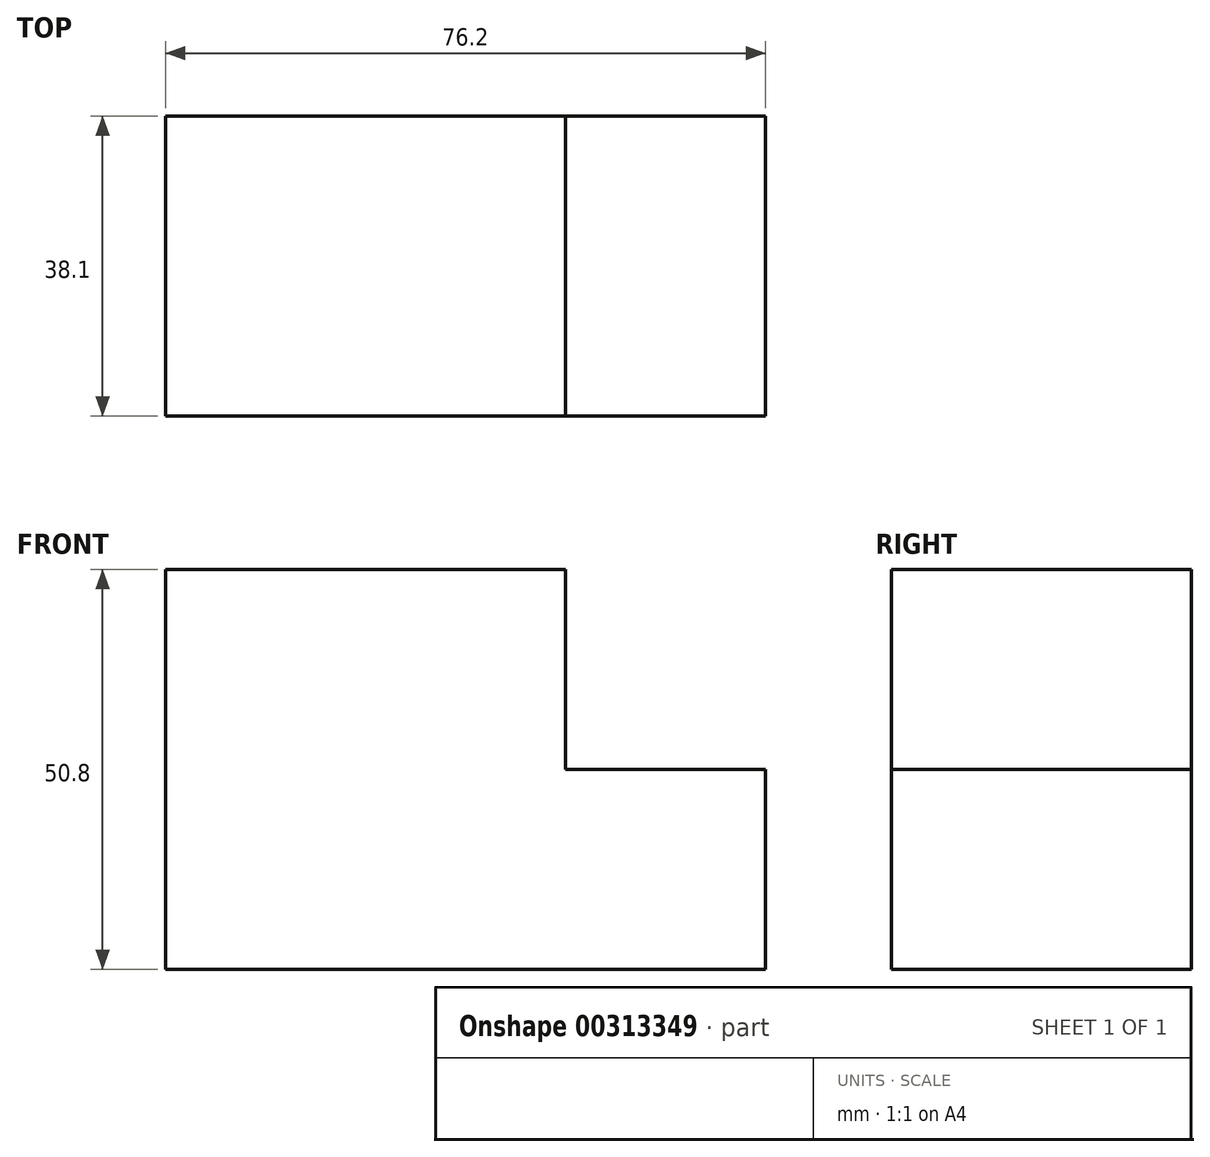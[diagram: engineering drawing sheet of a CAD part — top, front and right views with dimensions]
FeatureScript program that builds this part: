
annotation { "Feature Type Name" : "Feature", "Feature Type Description" : "" }
export const myFeature = defineFeature(function(context is Context, id is Id, definition is map)
    precondition{}
    {
        {
            var Q0;
            Q0=qCreatedBy(makeId("Front.planeOp"),FACE);
            var sketch = newSketch(context, id + "F0", { "sketchPlane" : qUnion([Q0])});
            skLineSegment(sketch, "E0", {"start": v(-37.44, -34.69) * mm, "end": v(38.76, -34.69) * mm});
            skLineSegment(sketch, "E1", {"start": v(38.76, -34.69) * mm, "end": v(38.76, -9.29) * mm});
            skLineSegment(sketch, "E2", {"start": v(38.76, -9.29) * mm, "end": v(13.36, -9.29) * mm});
            skLineSegment(sketch, "E3", {"start": v(13.36, -9.29) * mm, "end": v(13.36, 16.11) * mm});
            skLineSegment(sketch, "E4", {"start": v(13.36, 16.11) * mm, "end": v(-37.44, 16.11) * mm});
            skLineSegment(sketch, "E5", {"start": v(-37.44, 16.11) * mm, "end": v(-37.44, -34.69) * mm});
            skSolve(sketch);
        }
        {
            var Q0;
            Q0=makeQuery(id+"F0.imprint","IMPRINT",FACE,{"disambiguationData":[TD([[makeQuery(id+"F0.imprint","IMPRINT",EDGE,{"derivedFrom":sQuery(id+"F0.wireOp",EDGE,"E0")}),1.0]])]});
            extrude(context, id + "F1", {"entities" : qUnion([Q0]), "depth" : 38.1 * mm});
        }
    });
